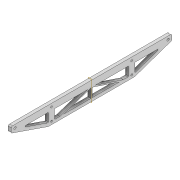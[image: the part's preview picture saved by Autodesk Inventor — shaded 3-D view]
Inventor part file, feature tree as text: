
AUTODESK INVENTOR PART (.ipt)
format: ipt  version: 2022 (Build 260153000, 153)  size: 190,976 bytes
history: native  units: mm
features: extrude x3, sketch x3, fillet x2, mirror x1
ambient origin geometry x8: Origin, YZ Plane, XZ Plane, XY Plane, X Axis, Y Axis, Z Axis, Center Point
bodies: Solid1 (feature_tree)
feature tree (9):
  extrude  "Extrusion1"  Depth=10.0mm
  fillet  "Fillet1"  Radius=3.9mm
  extrude  "Extrusion2"  Depth=3.9mm
  mirror  "Mirror1"
  extrude  "Extrusion3"  Depth=5.0mm TaperAngle=0.0deg
  fillet  "Fillet3"  Radius=2.0mm
  sketch  "Sketch1"  dims[d0=260.0mm d1=10.0mm d2=3.9mm]
  sketch  "Sketch2"  dims[d3=6.0mm d4=3.9mm]
  sketch  "Sketch4"  dims[d5=6.0mm d6=5.0mm d7=0.0mm d8=2.0mm d15=3.0mm d16=20.0mm d17=5.0mm d18=10.0mm d20=59.0mm d21=5.0mm d22=0.0mm d23=5.0mm d25=3.0mm d27=59.0mm d28=3.0mm d29=59.0mm d32=5.0mm d33=5.0mm d34=5.0mm d35=0.0mm d36=1.0mm d37=2.0mm d38=2.0mm d39=1.0mm d40=1.0mm]
